# Revit family: P200921MX-071c_MVWC565FW
name_source: partatom
category: Specialty Equipment
units: mm (PartAtom-declared; Revit-internal decimal feet)

## family parameters
Always vertical = Yes
Cut with Voids When Loaded = No
Enable Cutting in Views = No
Maintain Annotation Orientation = No
Part Type = Normal
Room Calculation Point = No
Round Connector Dimension = Use Diameter
Shared = No
Work Plane-Based = No

## types (1)
- MVWC565FW
    Amps = 0 A
    Back Panel Material = ARCAT - Metal - Aluminum
    Body Material = ARCAT - Metal - Steel - White
    Clearance Material = ARCAT - Clearance
    Default Elevation = 0"
    Depth = 27"
    Description = Top Load Washer with the Deep Water Wash Option and PowerWash® Cycle – 4.2 cu. ft.
Laveuse à chargement vertical avec programme PowerWash®, 4.9 pi3 C.E.I.
    Dimension Guide = http://access.whirlpool.com Guide&sku=MVWC565FW&language=EN
http://access.whirlpool.com Guide&sku=MVWC565FW&language=EN
    Door Material = ARCAT - Metal - Steel - White
    Energy Guide = http://access.whirlpool.com Guide&sku=MVWC565FW&language=EN
http://access.whirlpool.com Guide&sku=MVWC565FW&language=FR
    Family Name = Laundry
    Feature 1 = The Most Powerful Cleaning in its Class driven by PowerWash® cycle
Le meilleur nettoyage de sa catégorie, optimisé par le programme PowerWash® (parmi les marques dominantes de laveuses à chargement vertical dotées d’un agitateur et d'une capacité de 4 à 4,4 pi³, à programmes et réglages comparables, basé sur une brassée de 16 lb, utilisant le programme PowerWash®).
    Feature 2 = PowerWash® Cycle
Programme PowerWash®
    Feature 3 = PowerWash® Agitator
Agitateur PowerWash®
    Handle Material = ARCAT - Metal - Steel - White
    Height = 42"
    Installation-Fabrication = http://access.whirlpool.com Instruction&sku=MVWC565FW&language=EN
http://access.whirlpool.com Instruction&sku=MVWC565FW&language=FR
    Knob Material = ARCAT - Metal - Steel - Stainless
    Leg Material = ARCAT - Metal - Steel - Stainless
    Manufacturer = Maytag
    Model = MVWC565FW
    Voltage = 0 V
    Width = 27 1/2"

## geometry (parser evidence)
native form markers: Sweep x7
no freeform markers — native parametric forms only
